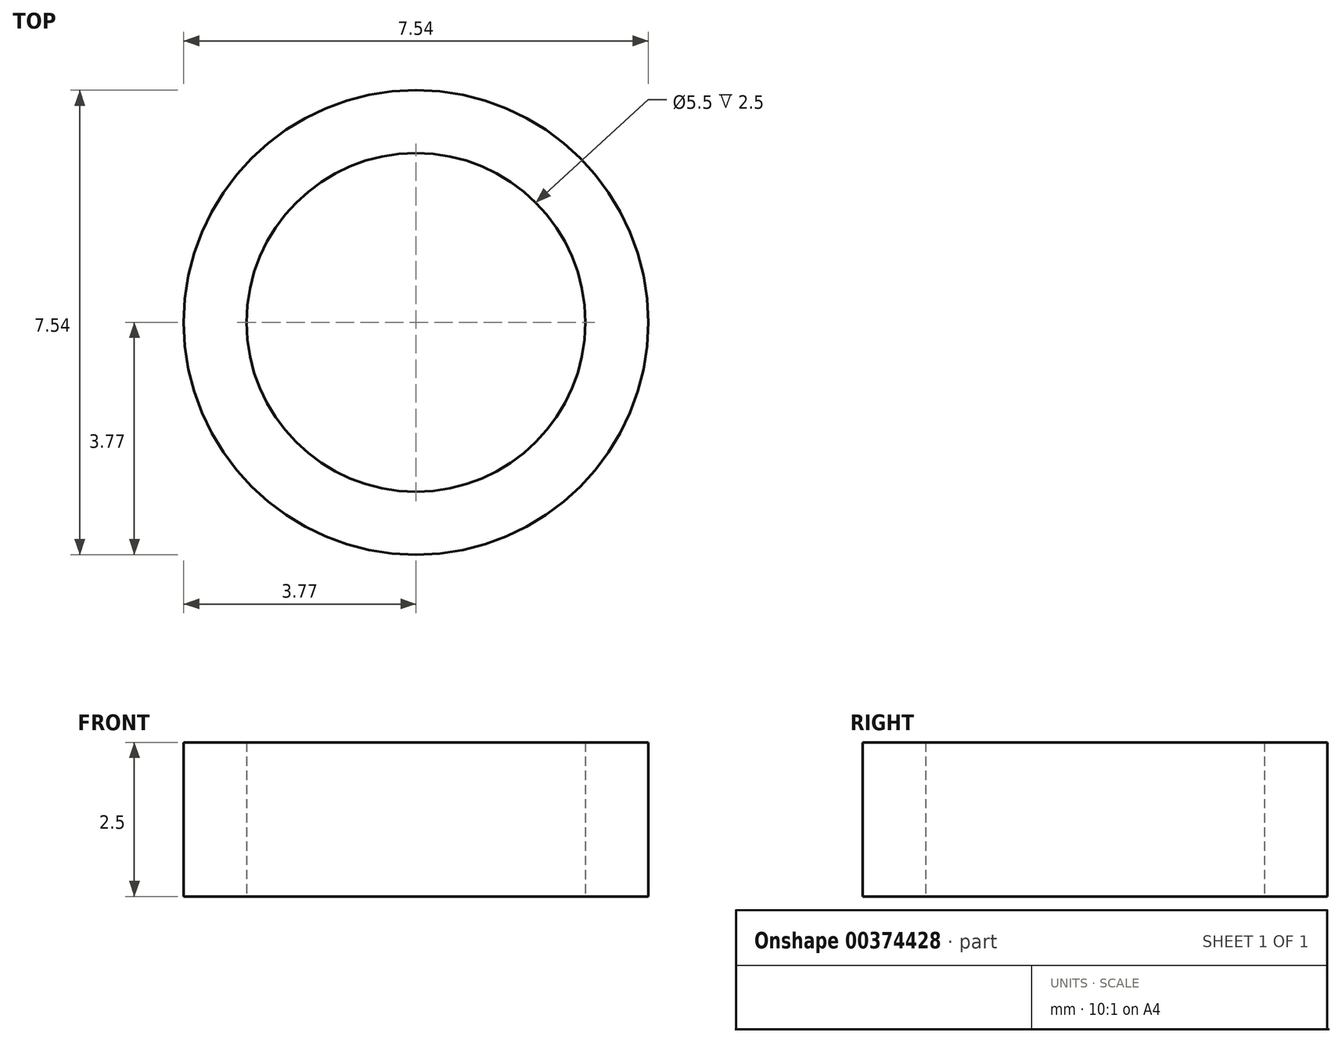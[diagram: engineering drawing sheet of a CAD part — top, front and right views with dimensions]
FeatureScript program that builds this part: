
annotation { "Feature Type Name" : "Feature", "Feature Type Description" : "" }
export const myFeature = defineFeature(function(context is Context, id is Id, definition is map)
    precondition{}
    {
        {
            var Q0;
            Q0=qCreatedBy(makeId("Top.planeOp"),FACE);
            var sketch = newSketch(context, id + "F0", { "sketchPlane" : qUnion([Q0])});
            skCircle(sketch, "E0", {"center": v(0, 0) * mm, "radius": 3.77 * mm});
            skCircle(sketch, "E1", {"center": v(0, 0) * mm, "radius": 2.75 * mm});
            skSolve(sketch);
        }
        {
            var Q0;
            Q0=qSketchRegion(id+"F0",true);
            extrude(context, id + "F1", {"entities" : qUnion([Q0]), "depth" : 2.5 * mm});
        }
    });
